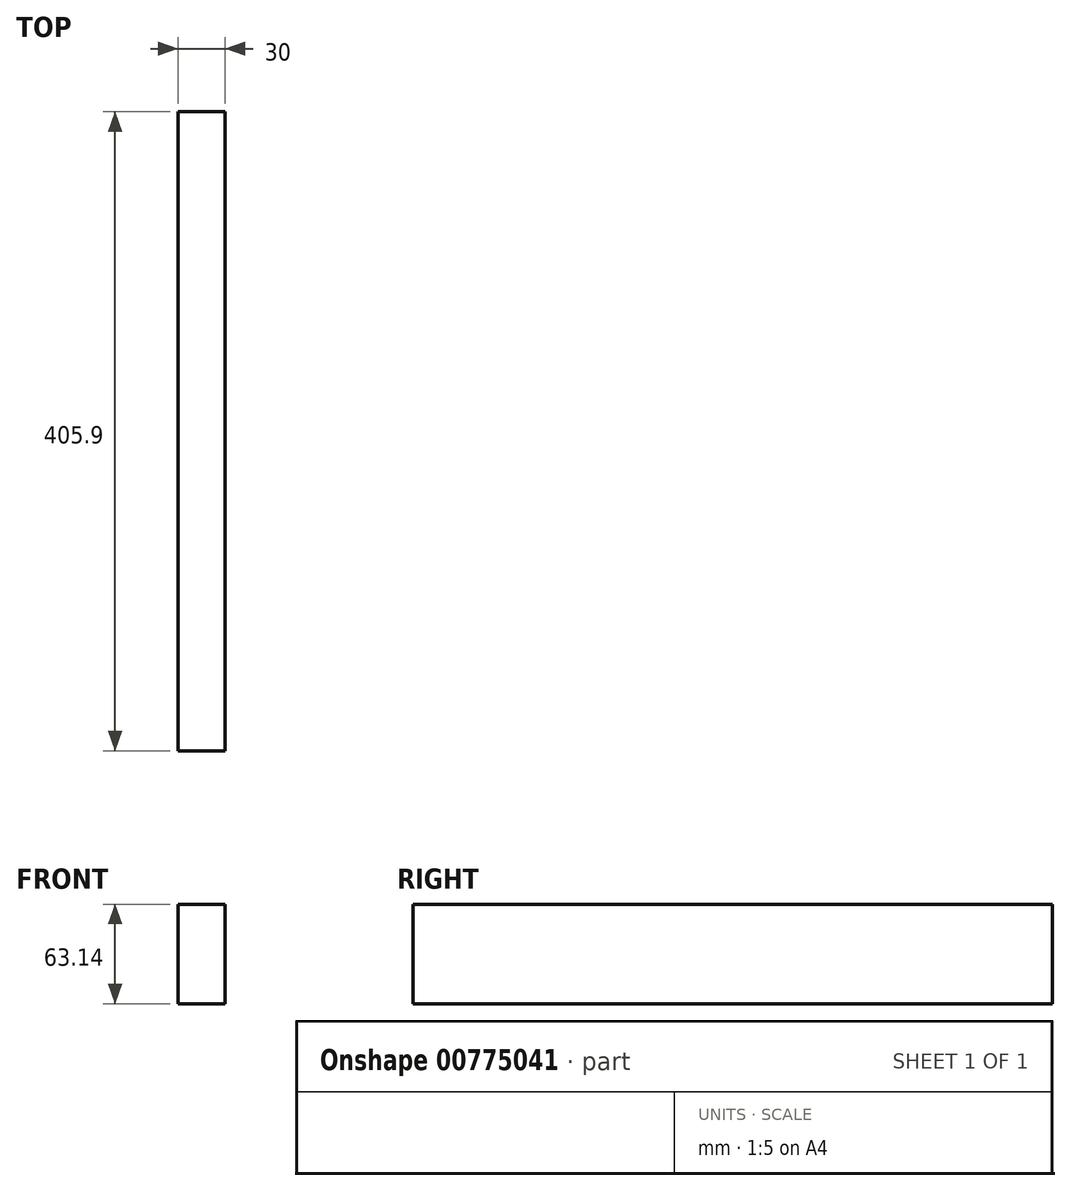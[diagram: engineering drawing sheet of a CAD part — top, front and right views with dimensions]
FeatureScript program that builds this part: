
annotation { "Feature Type Name" : "Feature", "Feature Type Description" : "" }
export const myFeature = defineFeature(function(context is Context, id is Id, definition is map)
    precondition{}
    {
        {
            var Q0;
            Q0=qCreatedBy(makeId("Right.planeOp"),FACE);
            var sketch = newSketch(context, id + "F0", { "sketchPlane" : qUnion([Q0])});
            skLineSegment(sketch, "E0.bottom", {"start": v(202.95, 44.9) * mm, "end": v(-202.95, 44.9) * mm});
            skLineSegment(sketch, "E0.top", {"start": v(202.95, -18.25) * mm, "end": v(-202.95, -18.25) * mm});
            skLineSegment(sketch, "E0.left", {"start": v(202.95, 44.9) * mm, "end": v(202.95, -18.25) * mm});
            skLineSegment(sketch, "E0.right", {"start": v(-202.95, 44.9) * mm, "end": v(-202.95, -18.25) * mm});
            skPoint(sketch, "E0.middle", {"position": v(0, 13.32) * mm});
            skSolve(sketch);
        }
        {
            var Q0;
            Q0=makeQuery(id+"F0.imprint","IMPRINT",FACE,{"disambiguationData":[TD([[makeQuery(id+"F0.imprint","IMPRINT",EDGE,{"derivedFrom":sQuery(id+"F0.wireOp",EDGE,"E0.bottom")}),1.0]])]});
            extrude(context, id + "F1", {"entities" : qUnion([Q0]), "depth" : 30 * mm, "offsetDistance" : 25 * mm});
        }
    });
